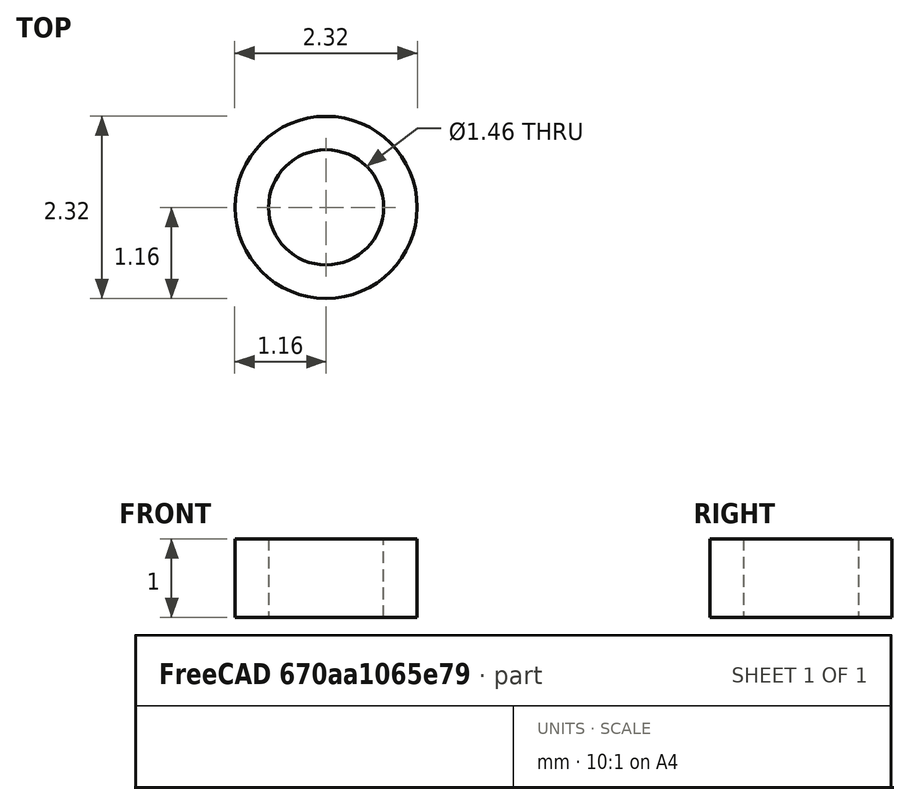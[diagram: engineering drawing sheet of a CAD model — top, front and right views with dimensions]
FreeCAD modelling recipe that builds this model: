
FCSTD DOCUMENT  (FreeCAD 0.19R24291 (Git))
Label: Path
License: All rights reserved
LicenseURL: http://en.wikipedia.org/wiki/All_rights_reserved
objects: Sketcher::SketchObject×1, PartDesign::Pad×1, PartDesign::Body×1
note: 4 computed .brp shape members not serialized (recipe doc carries the construction recipe); baked Part::Feature solids carry a one-line shape summary decoded from their .brp

FEATURE [Sketcher::SketchObject] Sketch
  FullyConstrained = false
  MapMode = 5
  Support = -> [XY_Plane]
  sketch-geometry (2):
    g0: Circle CenterX=0 CenterY=0 CenterZ=0 NormalX=0 NormalY=0 NormalZ=1 AngleXU=0 Radius=0.731229
    g1: Circle CenterX=0 CenterY=0 CenterZ=0 NormalX=0 NormalY=0 NormalZ=1 AngleXU=0 Radius=1.1563
  constraints (2):
    c: Coincident(g0,g-1)
    c: Coincident(g1,g0)
FEATURE [PartDesign::Pad] Pad
  Direction = (1,1,1)
  Length = 1
  Length2 = 100
  Profile = -> Sketch
  Type = 0
FEATURE [PartDesign::Body] Body
  Group = -> [Sketch,Pad]
  Origin = -> Origin
  Tip = -> Pad
